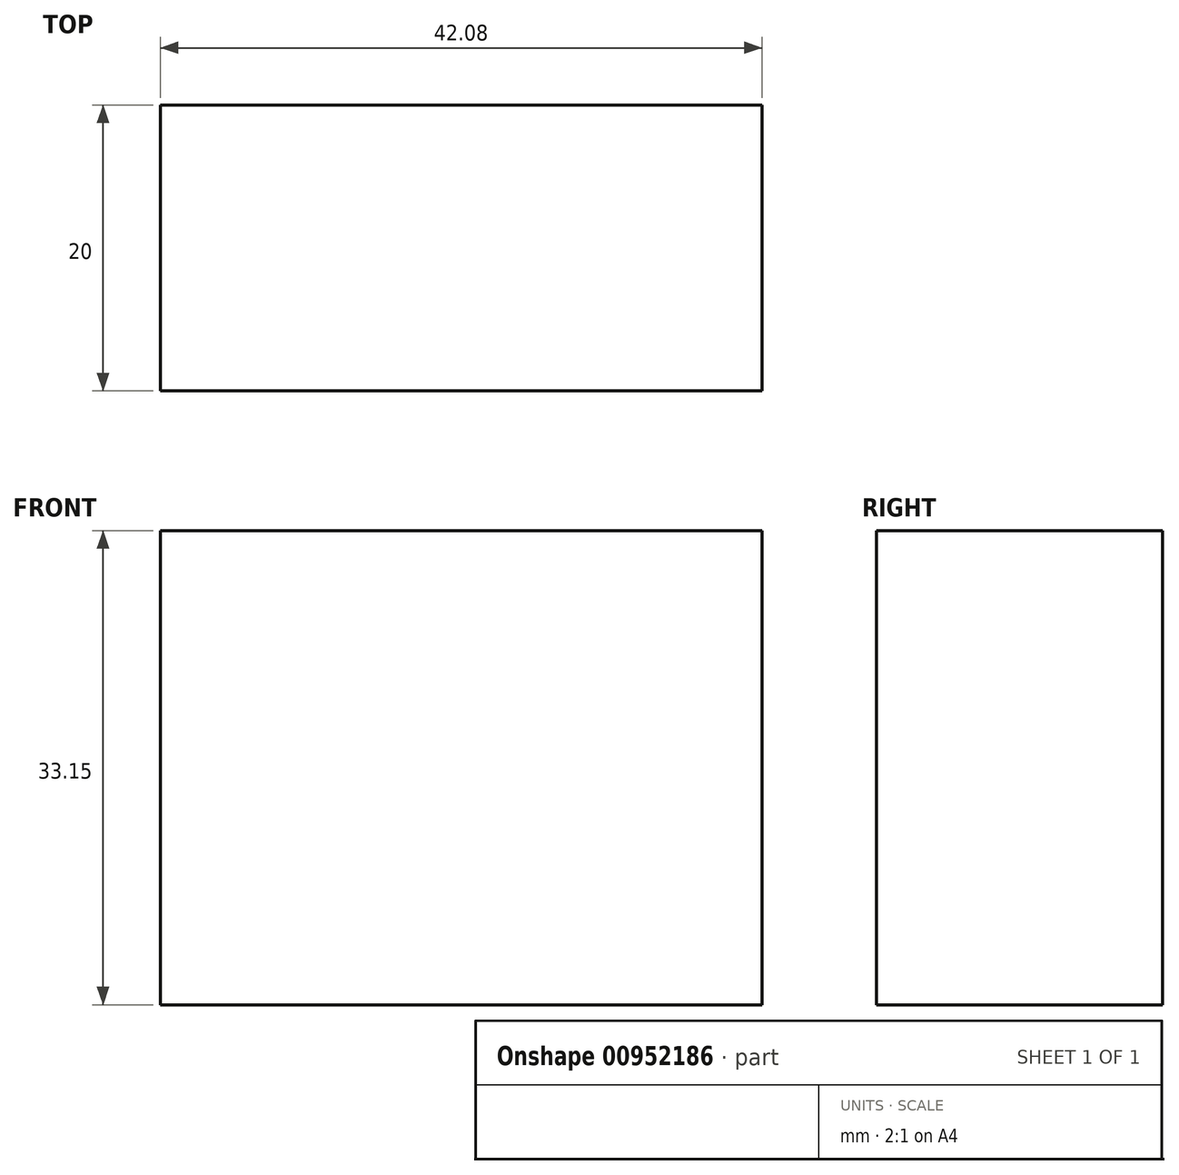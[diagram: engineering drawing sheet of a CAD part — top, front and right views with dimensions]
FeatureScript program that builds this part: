
annotation { "Feature Type Name" : "Feature", "Feature Type Description" : "" }
export const myFeature = defineFeature(function(context is Context, id is Id, definition is map)
    precondition{}
    {
        {
            assignVariable(context, id + "F0", {"name" : "R", "anyValue" : 20});
        }
        {
            var Q0;
            Q0=qCreatedBy(makeId("Front.planeOp"),FACE);
            var sketch = newSketch(context, id + "F1", { "sketchPlane" : qUnion([Q0])});
            skLineSegment(sketch, "E0.bottom", {"start": v(-97.17, 49.54) * mm, "end": v(-55.09, 49.54) * mm});
            skLineSegment(sketch, "E0.top", {"start": v(-97.17, 16.4) * mm, "end": v(-55.09, 16.4) * mm});
            skLineSegment(sketch, "E0.left", {"start": v(-97.17, 49.54) * mm, "end": v(-97.17, 16.4) * mm});
            skLineSegment(sketch, "E0.right", {"start": v(-55.09, 49.54) * mm, "end": v(-55.09, 16.4) * mm});
            skSolve(sketch);
        }
        {
            var Q0;
            Q0 = qSketchRegion(id + "F1", true);
            extrude(context, id + "F2", {"entities" : qUnion([Q0]), "depth" : (getVariable(context, 'R')) * mm, "offsetDistance" : 25 * mm});
        }
    });
